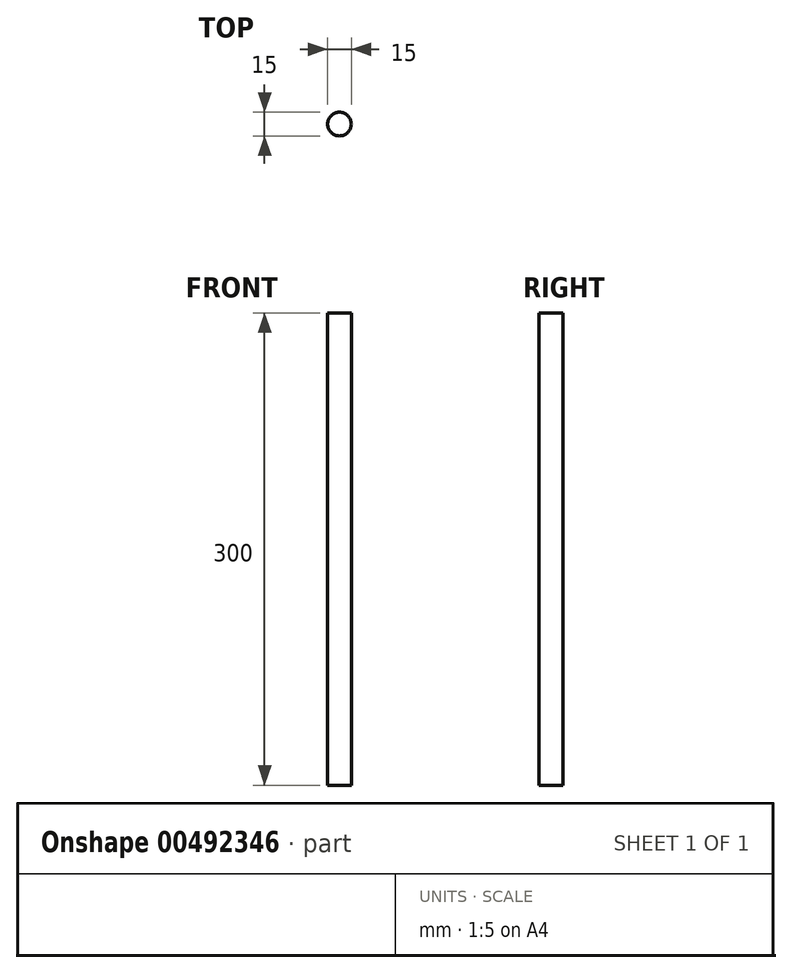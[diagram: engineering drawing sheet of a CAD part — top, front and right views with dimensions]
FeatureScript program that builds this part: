
annotation { "Feature Type Name" : "Feature", "Feature Type Description" : "" }
export const myFeature = defineFeature(function(context is Context, id is Id, definition is map)
    precondition{}
    {
        {
            var Q0;
            Q0=qCreatedBy(makeId("Top.planeOp"),FACE);
            var sketch = newSketch(context, id + "F0", { "sketchPlane" : qUnion([Q0])});
            skCircle(sketch, "E0", {"center": v(0, 0) * mm, "radius": 7.5 * mm});
            skSolve(sketch);
        }
        {
            var Q0;
            Q0=makeQuery(id+"F0.imprint","IMPRINT",FACE,{"disambiguationData":[TD([[makeQuery(id+"F0.imprint","IMPRINT",EDGE,{"derivedFrom":sQuery(id+"F0.wireOp",EDGE,"E0")}),1.0]])]});
            extrude(context, id + "F1", {"entities" : qUnion([Q0]), "depth" : 300 * mm});
        }
    });
